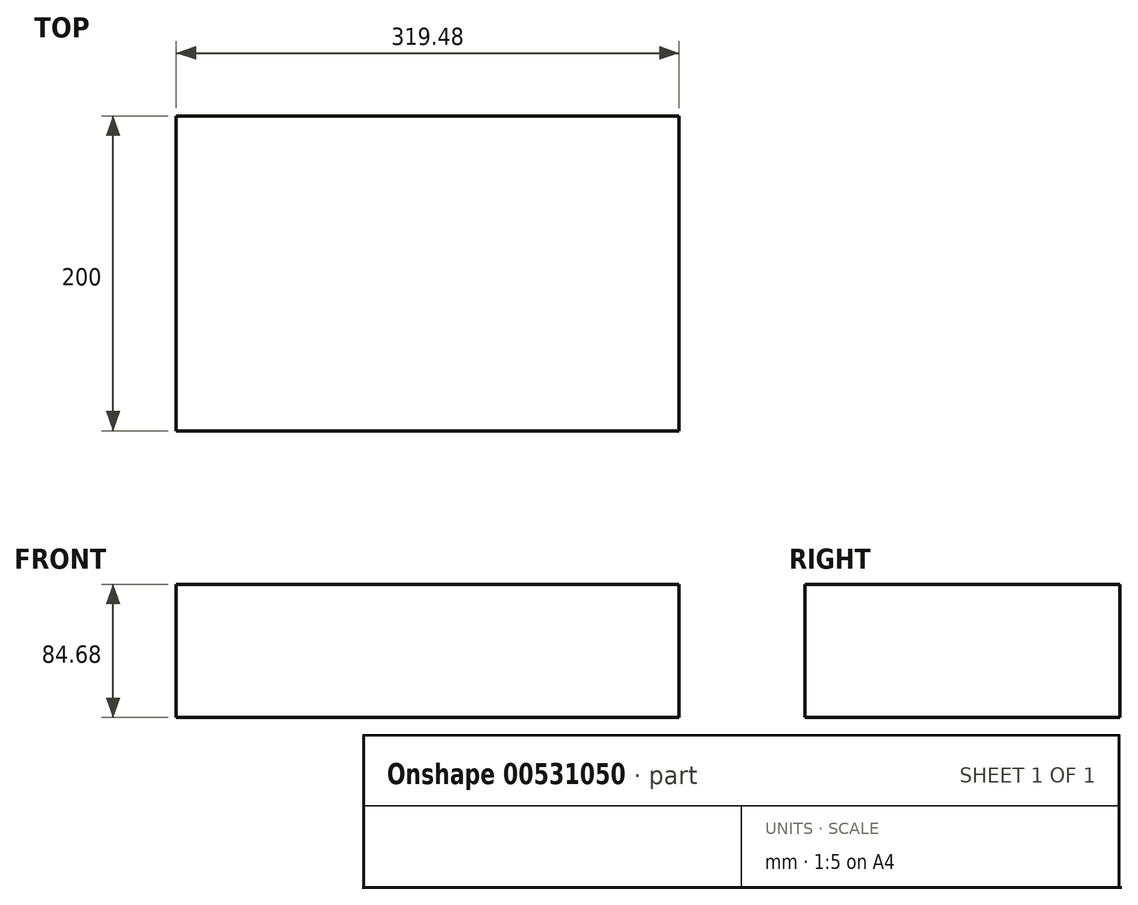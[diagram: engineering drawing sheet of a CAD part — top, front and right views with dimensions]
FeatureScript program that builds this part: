
annotation { "Feature Type Name" : "Feature", "Feature Type Description" : "" }
export const myFeature = defineFeature(function(context is Context, id is Id, definition is map)
    precondition{}
    {
        {
            var Q0;
            Q0=qCreatedBy(makeId("Front.planeOp"),FACE);
            var sketch = newSketch(context, id + "F0", { "sketchPlane" : qUnion([Q0])});
            skLineSegment(sketch, "E0.bottom", {"start": v(-159.74, 42.34) * mm, "end": v(159.74, 42.34) * mm});
            skLineSegment(sketch, "E0.top", {"start": v(-159.74, -42.34) * mm, "end": v(159.74, -42.34) * mm});
            skLineSegment(sketch, "E0.left", {"start": v(-159.74, 42.34) * mm, "end": v(-159.74, -42.34) * mm});
            skLineSegment(sketch, "E0.right", {"start": v(159.74, 42.34) * mm, "end": v(159.74, -42.34) * mm});
            skPoint(sketch, "E0.middle", {"position": v(0, 0) * mm});
            skSolve(sketch);
        }
        {
            var Q0;
            Q0 = qSketchRegion(id + "F0", true);
            extrude(context, id + "F1", {"entities" : qUnion([Q0]), "oppositeDirection" : true, "depth" : 200 * mm, "offsetDistance" : 25 * mm});
        }
    });
